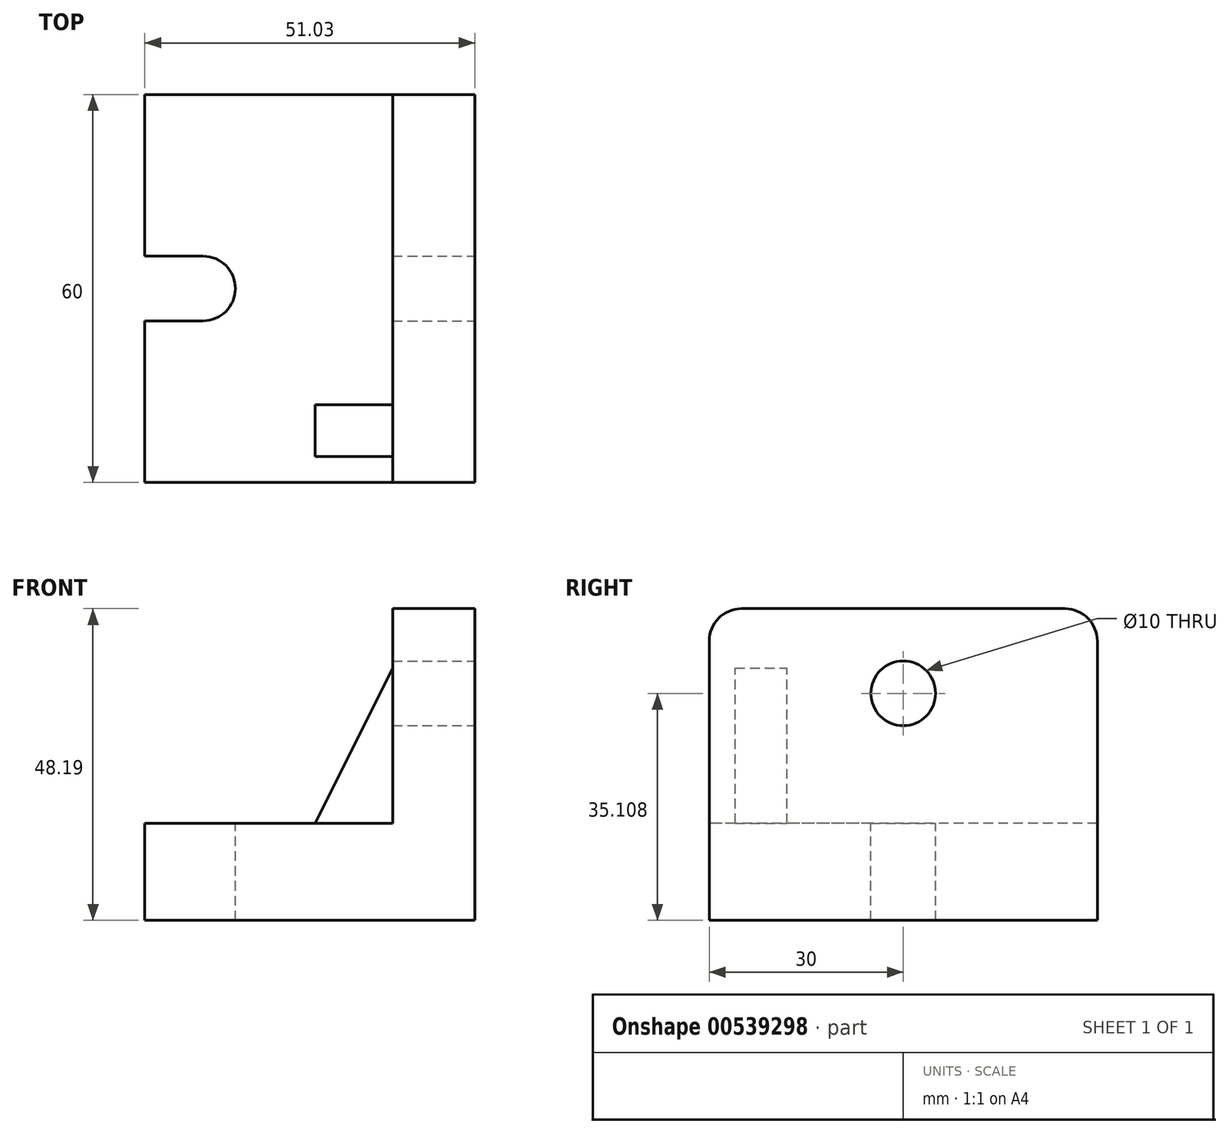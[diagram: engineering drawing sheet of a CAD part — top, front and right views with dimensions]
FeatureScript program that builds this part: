
annotation { "Feature Type Name" : "Feature", "Feature Type Description" : "" }
export const myFeature = defineFeature(function(context is Context, id is Id, definition is map)
    precondition{}
    {
        {
            var Q0;
            Q0=qCreatedBy(makeId("Front.planeOp"),FACE);
            var sketch = newSketch(context, id + "F0", { "sketchPlane" : qUnion([Q0])});
            skLineSegment(sketch, "E0", {"start": v(-51.03, 0) * mm, "end": v(-51.03, 15) * mm});
            skLineSegment(sketch, "E1", {"start": v(-51.03, 15) * mm, "end": v(-12.7, 15) * mm});
            skLineSegment(sketch, "E2", {"start": v(-12.7, 15) * mm, "end": v(-12.7, 48.2) * mm});
            skLineSegment(sketch, "E3", {"start": v(-12.7, 48.2) * mm, "end": v(0, 48.2) * mm});
            skLineSegment(sketch, "E4", {"start": v(0, 48.2) * mm, "end": v(0, 0) * mm});
            skLineSegment(sketch, "E5", {"start": v(-51.03, 0) * mm, "end": v(0, 0) * mm});
            skSolve(sketch);
        }
        {
            var Q0;
            Q0 = qSketchRegion(id + "F0", true);
            extrude(context, id + "F1", {"entities" : qUnion([Q0]), "endBound" : BoundingType.SYMMETRIC, "oppositeDirection" : true, "depth" : 60 * mm, "offsetDistance" : 25 * mm});
        }
        {
            var Q0;
            Q0=makeQuery(id+"F1.opExtrude","SWEPT_FACE",FACE,{"disambiguationData":[OSD([sQuery(id+"F0.wireOp",EDGE,"E4")])]});
            var sketch = newSketch(context, id + "F2", { "sketchPlane" : qUnion([Q0])});
            skCircle(sketch, "E6", {"center": v(0, 35.1) * mm, "radius": 5 * mm});
            skPoint(sketch, "E6.centerSnap0", {"position": v(0, 48.2) * mm});
            skSolve(sketch);
        }
        {
            var Q0;
            Q0=makeQuery(id+"F2.imprint","IMPRINT",FACE,{"disambiguationData":[TD([[makeQuery(id+"F2.imprint","IMPRINT",EDGE,{"derivedFrom":sQuery(id+"F2.wireOp",EDGE,"E6")}),1.0]])]});
            extrude(context, id + "F3", {"entities" : qUnion([Q0]), "operationType" : NewBodyOperationType.REMOVE, "endBound" : BoundingType.UP_TO_NEXT, "oppositeDirection" : true, "depth" : 25 * mm, "offsetDistance" : 25 * mm});
        }
        {
            var Q0;
            Q0=makeQuery(id+"F1.opExtrude","SWEPT_FACE",FACE,{"disambiguationData":[OSD([sQuery(id+"F0.wireOp",EDGE,"E1")])]});
            var sketch = newSketch(context, id + "F4", { "sketchPlane" : qUnion([Q0])});
            skCircle(sketch, "E7", {"center": v(-42.03, 0) * mm, "radius": 5 * mm});
            skPoint(sketch, "E7.centerSnap0", {"position": v(-51.03, 0) * mm});
            skLineSegment(sketch, "E8", {"start": v(-42.03, -5) * mm, "end": v(-51.03, -5) * mm});
            skLineSegment(sketch, "E9", {"start": v(-42.03, 5) * mm, "end": v(-51.03, 5) * mm});
            skLineSegment(sketch, "E10", {"start": v(-51.03, 5) * mm, "end": v(-51.03, -5) * mm});
            skSolve(sketch);
        }
        {
            var Q0;
            Q0 = qSketchRegion(id + "F4", true);
            var Q1;
            Q1=makeQuery(id+"F1.opExtrude","SWEPT_FACE",FACE,{"disambiguationData":[OSD([sQuery(id+"F0.wireOp",EDGE,"E5")])]});
            extrude(context, id + "F5", {"entities" : qUnion([Q0]), "operationType" : NewBodyOperationType.REMOVE, "endBound" : BoundingType.UP_TO_SURFACE, "oppositeDirection" : true, "depth" : 25 * mm, "endBoundEntityFace" : qUnion([Q1]), "offsetDistance" : 25 * mm});
        }
        {
            var Q0;
            Q0=qCreatedBy(makeId("Front.planeOp"),FACE);
            cPlane(context, id + "F6", {"entities" : qUnion([Q0]), "cplaneType" : CPlaneType.OFFSET, "offset" : 18 * mm, "width" : 150 * mm, "height" : 150 * mm});
        }
        {
            var Q0;
            Q0=qCreatedBy(id+"F6.planeOp",FACE);
            var sketch = newSketch(context, id + "F7", { "sketchPlane" : qUnion([Q0])});
            skLineSegment(sketch, "E11.0", {"start": v(-24.7, 15) * mm, "end": v(-12.7, 15) * mm});
            skLineSegment(sketch, "E12.0", {"start": v(-12.7, 15) * mm, "end": v(-12.7, 39) * mm});
            skLineSegment(sketch, "E13", {"start": v(-12.7, 39) * mm, "end": v(-24.7, 15) * mm});
            skSolve(sketch);
        }
        {
            var Q0;
            Q0 = qSketchRegion(id + "F7", true);
            extrude(context, id + "F8", {"entities" : qUnion([Q0]), "operationType" : NewBodyOperationType.ADD, "depth" : 8 * mm, "offsetDistance" : 25 * mm});
        }
        {
            var Q0;
            Q0=makeQuery(id+"F1.opExtrude","SWEPT_FACE",FACE,{"disambiguationData":[OSD([sQuery(id+"F0.wireOp",EDGE,"E2")])]});
            var sketch = newSketch(context, id + "F9", { "sketchPlane" : qUnion([Q0])});
            skCircle(sketch, "E14", {"center": v(0, 35.1) * mm, "radius": 8 * mm});
            skSolve(sketch);
        }
        {
            var Q0;
            Q0=sQuery(id+"F9.wireOp",EDGE,"E14");
            extrude(context, id + "F10", {"bodyType" : ToolBodyType.SURFACE, "surfaceEntities" : qUnion([Q0]), "oppositeDirection" : true, "depth" : 9.3 * mm, "offsetDistance" : 25 * mm});
        }
        {
            var Q0;
            Q0=makeQuery(id+"F1.opExtrude","CAP_EDGE",EDGE,{"disambiguationData":[OSD([sQuery(id+"F0.wireOp",EDGE,"E3")])],"isStart":false});
            var Q1;
            Q1=makeQuery(id+"F1.opExtrude","CAP_EDGE",EDGE,{"disambiguationData":[OSD([sQuery(id+"F0.wireOp",EDGE,"E3")])],"isStart":true});
            fillet(context, id + "F11", {"entities" : qUnion([Q0, Q1]), "radius" : 5 * mm, "tangentPropagation" : true, "allowEdgeOverflow" : false});
        }
    });
